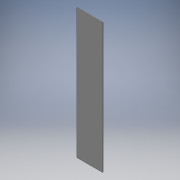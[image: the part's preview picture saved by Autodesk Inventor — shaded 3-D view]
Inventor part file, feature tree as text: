
AUTODESK INVENTOR PART (.ipt)
format: ipt  version: 2016 (Build 200138000, 138)  size: 91,136 bytes
history: native  units: mm
features: extrude x1, sketch x1
ambient origin geometry x8: Origin, YZ Plane, XZ Plane, XY Plane, X Axis, Y Axis, Z Axis, Center Point
bodies: Solid1 (feature_tree)
feature tree (2):
  extrude  "Extrusion1"  Depth=220.0mm
  sketch  "Sketch1"  dims[d0=1120.0mm d1=220.0mm d2=5.0mm d3=0.0mm]
